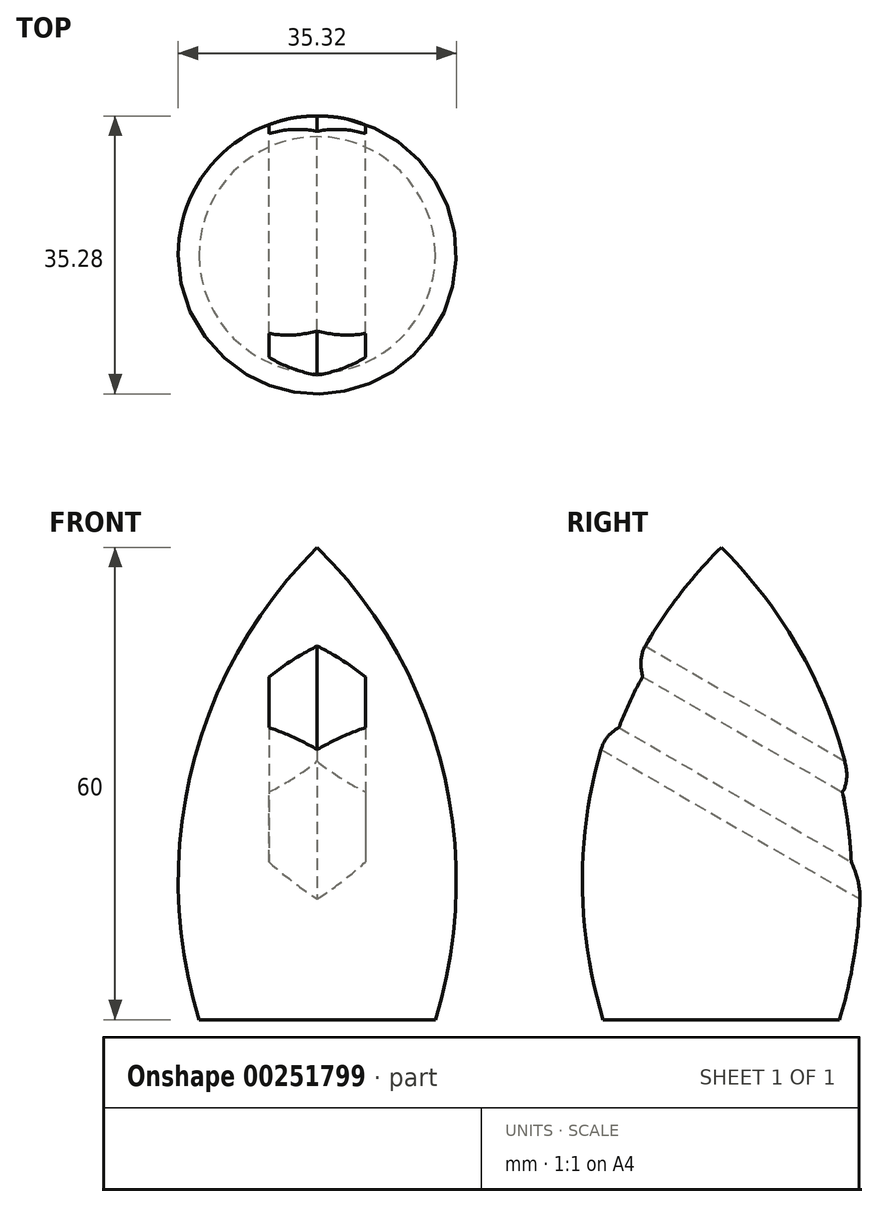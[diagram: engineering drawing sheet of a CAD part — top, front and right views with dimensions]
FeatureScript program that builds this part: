
annotation { "Feature Type Name" : "Feature", "Feature Type Description" : "" }
export const myFeature = defineFeature(function(context is Context, id is Id, definition is map)
    precondition{}
    {
        {
            var Q0;
            Q0=qCreatedBy(makeId("Front.planeOp"),FACE);
            var sketch = newSketch(context, id + "F0", { "sketchPlane" : qUnion([Q0])});
            skLineSegment(sketch, "E0", {"start": v(0, 0) * mm, "end": v(15, 0) * mm});
            skPoint(sketch, "E1.0.midPoint", {"position": v(-3.12, 28.2) * mm});
            skPoint(sketch, "E1.1.start.orphan", {"position": v(-6.23, 30) * mm});
            skPoint(sketch, "E2.trimOffspring.start.orphan", {"position": v(0, 26.4) * mm});
            skLineSegment(sketch, "E3", {"start": v(0, 60) * mm, "end": v(0, 0) * mm});
            skArc(sketch, "E4", {"start": v(15, 0) * mm, "mid": v(15.88, 32.1) * mm, "end": v(0, 60) * mm});
            skSolve(sketch);
        }
        {
            var Q0;
            Q0=makeQuery(id+"F0.imprint","IMPRINT",FACE,{"disambiguationData":[TD([[makeQuery(id+"F0.imprint","IMPRINT",EDGE,{"derivedFrom":sQuery(id+"F0.wireOp",EDGE,"E0")}),1.0]])]});
            var Q1;
            Q1=sQuery(id+"F0.wireOp",EDGE,"E3");
            revolve(context, id + "F1", {"entities" : qUnion([Q0]), "axis" : qUnion([Q1]), "revolveType" : RevolveType.FULL});
        }
        {
            var Q0;
            Q0=qCreatedBy(makeId("Front.planeOp"),FACE);
            var sketch = newSketch(context, id + "F2", { "sketchPlane" : qUnion([Q0])});
            skLineSegment(sketch, "E5", {"start": v(-19.55, 50.99) * mm, "end": v(-19.55, 0) * mm});
            skLineSegment(sketch, "E6", {"start": v(-19.55, 0) * mm, "end": v(45.32, 0) * mm});
            skSolve(sketch);
        }
        {
            var Q0;
            Q0=sQuery(id+"F2.wireOp",EDGE,"E6");
            var Q1;
            Q1=sQuery(id+"F2.wireOp",EDGE,"E5");
            cPlane(context, id + "F3", {"entities" : qUnion([Q0, Q1]), "cplaneType" : CPlaneType.LINE_ANGLE, "offset" : 25 * mm, "angle" : 30 * degree, "oppositeDirection" : true, "width" : 150 * mm, "height" : 150 * mm});
        }
        {
            var Q0;
            Q0=qCreatedBy(id+"F3.planeOp",FACE);
            var sketch = newSketch(context, id + "F4", { "sketchPlane" : qUnion([Q0])});
            skLineSegment(sketch, "E7.0", {"start": v(0, 22.08) * mm, "end": v(-6.15, 25.63) * mm});
            skLineSegment(sketch, "E7.1", {"start": v(-6.15, 25.63) * mm, "end": v(-6.15, 32.73) * mm});
            skLineSegment(sketch, "E7.2", {"start": v(-6.15, 32.73) * mm, "end": v(0, 36.28) * mm});
            skLineSegment(sketch, "E7.3", {"start": v(0, 36.28) * mm, "end": v(6.15, 32.73) * mm});
            skLineSegment(sketch, "E7.4", {"start": v(6.15, 32.73) * mm, "end": v(6.15, 25.63) * mm});
            skLineSegment(sketch, "E7.5", {"start": v(6.15, 25.63) * mm, "end": v(0, 22.08) * mm});
            skPoint(sketch, "E7.0.midPoint", {"position": v(-3.07, 23.86) * mm});
            skPoint(sketch, "E7.cCircle.center.orphan", {"position": v(0, 29.18) * mm});
            skSolve(sketch);
        }
        {
            var Q0;
            Q0 = qSketchRegion(id + "F4", true);
            extrude(context, id + "F5", {"entities" : qUnion([Q0]), "operationType" : NewBodyOperationType.REMOVE, "endBound" : BoundingType.THROUGH_ALL, "oppositeDirection" : true, "depth" : 25 * mm});
        }
        {
            var Q0;
            Q0=makeQuery(id+"F5.boolean.opBoolean","COPY",FACE,{"derivedFrom":makeQuery(id+"F5.opExtrude","CAP_FACE",FACE,{"disambiguationData":[OSD([sQuery(id+"F4.wireOp",EDGE,"E7.0"),sQuery(id+"F4.wireOp",EDGE,"E7.1"),sQuery(id+"F4.wireOp",EDGE,"E7.2"),sQuery(id+"F4.wireOp",EDGE,"E7.3"),sQuery(id+"F4.wireOp",EDGE,"E7.4"),sQuery(id+"F4.wireOp",EDGE,"E7.5")])],"isStart":true})});
            extrude(context, id + "F6", {"entities" : qUnion([Q0]), "operationType" : NewBodyOperationType.REMOVE, "endBound" : BoundingType.THROUGH_ALL, "oppositeDirection" : true, "depth" : 25 * mm});
        }
    });
